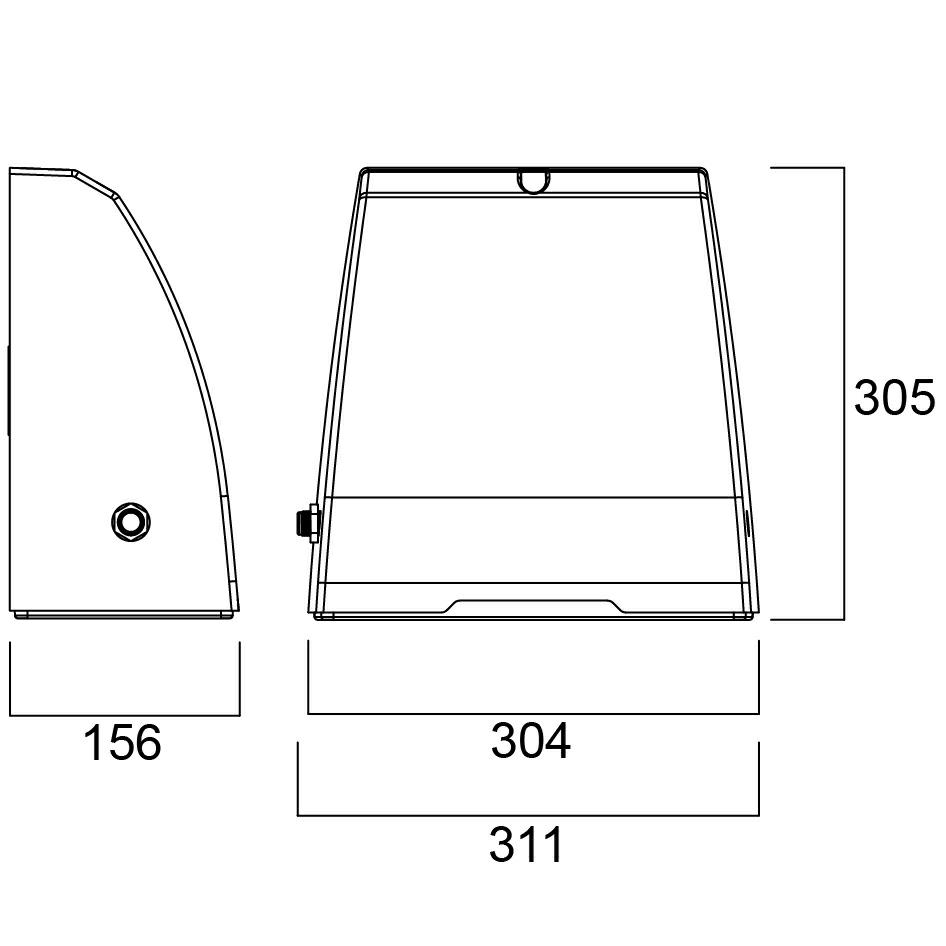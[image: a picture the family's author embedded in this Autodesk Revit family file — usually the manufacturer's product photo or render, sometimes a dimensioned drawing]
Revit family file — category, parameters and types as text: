
# Revit family: 0049945_2750lm
name_source: partatom
category: Lighting Fixtures
revit_build: Autodesk Revit 2018 (Build: 20170223_1515(x64)
units: mm (PartAtom-declared; Revit-internal decimal feet)

## family parameters
Cut with Voids When Loaded = No
Host = Face
Light Source = Yes
OmniClass Number = 23.80.70.00
OmniClass Title = Lighting
Part Type = Normal
Room Calculation Point = No
Round Connector Dimension = Use Diameter
Shared = No

## types (1)
- 0049945 MURO SURF IP65 1700-3250LM 840 PH E3 GR
    Apparent Load = 30 VA
    Assembly Code = D5020200
    AssetType = Fixed
    ClassificationName = Uniclass2015
    ClassificationValue = EF_70_80
    Color Filter = 16777215
    Cost = 0 $
    Default Elevation = 1219 mm
    Description = Muro Surface is a wall mounted fixture for exterior lighting applications with 3 hours combined non-maintained emergency unit. Comes with aluminium housing in RAL7016 anthracite grey colour, frosted PC diffuser, IP65, IK10, Class I, 4000K, non-dimmable multipower driver with 5 settings, 1700 / 1900 / 2750 / 3150 / 3250 lm, 16 / 18 / 26 / 29 / 30 W, up to 109 lm/W total system efficacy, switchable built in Mini photocell, CRI80, Asymmetrical beam, 119.000 hrs L70B50 lifespan, 304 x 305 x 155 mm (L x W x D) dimensions, 4.32 kg weight.
    Dimming Lamp Color Temperature Shift = <None>
    DocumentationLiterature = http://www.sylvania-lighting.com
    ElectricShockClassification = 108
    Emit Shape Visible in Rendering = No
    Emit from Circle Diameter = 610 mm
    IfcExportAs = Class I
    IfcExportType = IfcLightFixtureType
    ImpactProtectionIndex = IfcLightFixtureType
    IngressProtection = IfcLightFixtureType
    InputNominalFrequency = 4000
    InputVoltage = 0
    LampColourRenderingIndex = 16500
    LampColourTemperature = LED
    LampMacAdamStep = 80
    LampNominalLuminous = 4000 K
    LightOutputRatio = LED
    LuminaireType = 0
    ManufacturerName = 108 lm/W
    Material = Feilo Sylvania
    Material_1_SYL = <By Category>
    Material_2_SYL = <By Category>
    Material_3_SYL = <By Category>
    Material_4_SYL = <By Category>
    Model = Muro Surface IP65 1700-3250lm 840 PH E3 Grey
    ModelNumber = 0049945
    ModelReference = Muro Surface IP65 1700-3250lm 840 PH E3 Grey
    Name = Muro Surface IP65 1700-3250lm 840 PH E3 Grey
    NominalDepth = 155 mm  [stored 0.50853 ft]
    NominalHeight = 305 mm  [stored 1.00066 ft]
    NominalLength = 155 mm  [stored 0.50853 ft]
    Photometric Web File = 0049945_2750lm.IES
    PowerConsumption = Lighting
    PowerFactor = 0.95
    Tilt Angle = -90.00°
    Type Image = <None>
    TypeName = Muro Surface IP65 1700-3250lm 840 PH E3 Grey
    URL = 0.9
    Voltage = 0 V
    WarrantyDescription = http://www.sylvania-lighting.com

note: [stored X ft] marks values corroborated as IEEE doubles in the binary element streams (Revit-internal decimal feet)

## geometry (parser evidence)
native form markers: Sweep x1
no freeform markers — native parametric forms only
